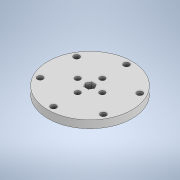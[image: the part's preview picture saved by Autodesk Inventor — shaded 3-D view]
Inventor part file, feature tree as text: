
AUTODESK INVENTOR PART (.ipt)
format: ipt  version: 2020 (Build 240168000, 168)  size: 158,208 bytes
history: native  units: in
note: dims shown in document units (in); Inventor stores cm internally (conversion verified against a paired STEP export)
features: extrude x5, sketch x5, plane x2, pattern_circular x2, other x1
ambient origin geometry x8: Origin, YZ Plane, XZ Plane, XY Plane, X Axis, Y Axis, Z Axis, Center Point
bodies: Solid1 (feature_tree)
feature tree (15):
  extrude  "Extrusion1"  Depth=0.3in TaperAngle=0.0deg
  plane  "Work Plane5"
  extrude  "Extrusion4"  Depth=1.0in TaperAngle=0.0deg
  extrude  "Extrusion5"  Depth=0.075in
  plane  "Work Plane6"
  other  "Work Axis1"
  pattern_circular  "Circular Pattern1"  Count=6 Angle=360.0deg
  extrude  "Extrusion6"  Depth=0.07in
  pattern_circular  "Circular Pattern2"  [2 undecoded]
  extrude  "Extrusion8"  Depth=0.07in TaperAngle=360.0deg
  sketch  "Sketch1"  dims[d0=2.2in d1=0.3in d2=0.0in]
  sketch  "Sketch5"  dims[d10=0.105in d11=1.0in d12=0.0in]
  sketch  "Sketch6"  dims[d13=0.07in d14=0.075in]
  sketch  "Sketch8"  dims[d15=1.0in d16=0.0in d17=2.3622in d18=360.0deg]
  sketch  "Sketch10"  dims[d20=0.13in d21=0.07in d22=1.0in d23=0.0in d24=1.5748in d25=360.0deg d30=0.1in d31=0.0in d27=0.5in d28=0.0344in d29=0.5in]
note: 2 required parameter values undecoded (feature->parameter linkage not recoverable at this tier; creation-order binding heuristic only, values carry confidence <= 0.55)
